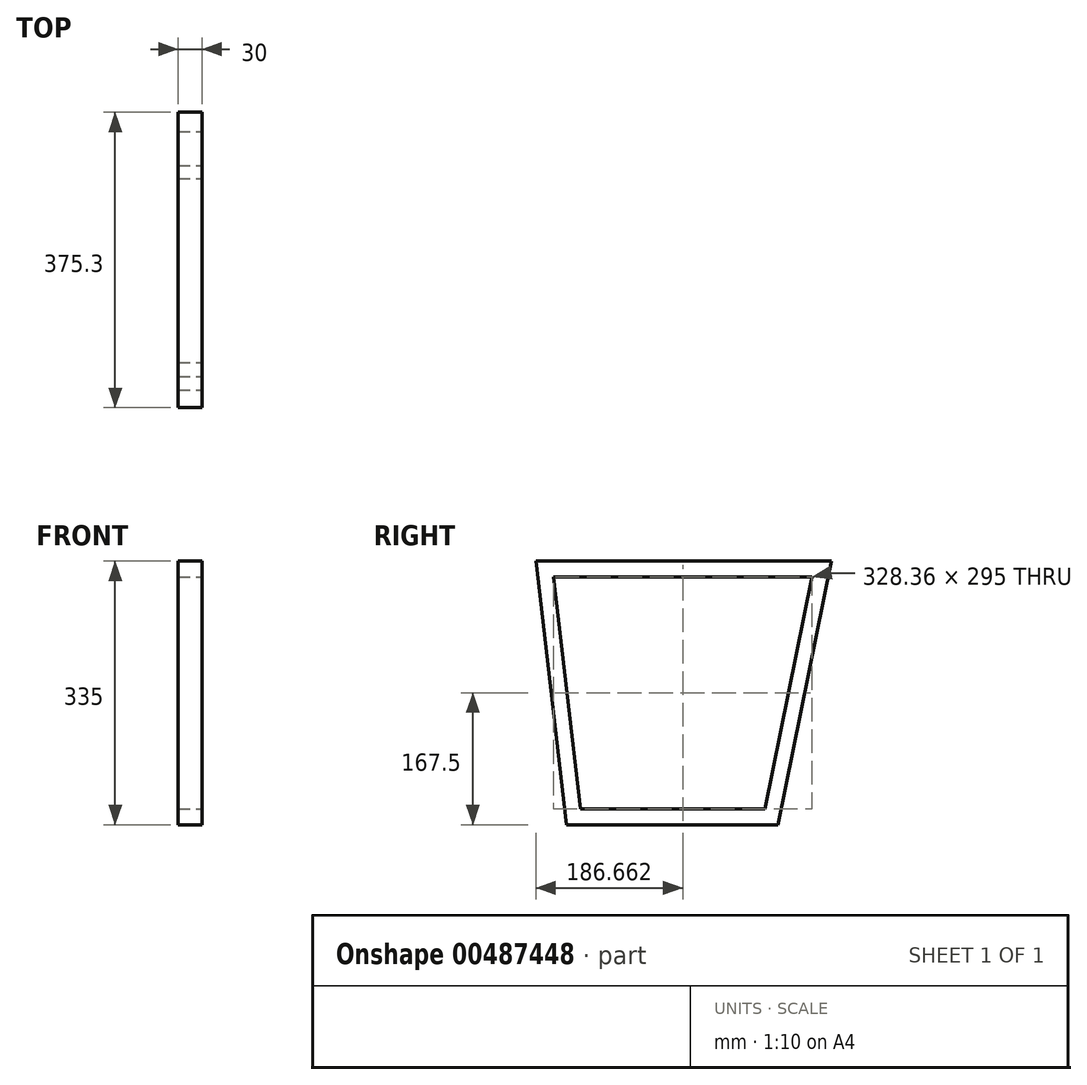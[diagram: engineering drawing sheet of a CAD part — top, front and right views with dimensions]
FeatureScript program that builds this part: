
annotation { "Feature Type Name" : "Feature", "Feature Type Description" : "" }
export const myFeature = defineFeature(function(context is Context, id is Id, definition is map)
    precondition{}
    {
        {
            var Q0;
            Q0=qCreatedBy(makeId("Right.planeOp"),FACE);
            var sketch = newSketch(context, id + "F0", { "sketchPlane" : qUnion([Q0])});
            skLineSegment(sketch, "E0", {"start": v(467.6, 335) * mm, "end": v(92.29, 335) * mm});
            skLineSegment(sketch, "E1", {"start": v(92.29, 335) * mm, "end": v(131.58, 0) * mm});
            skLineSegment(sketch, "E2", {"start": v(467.6, 335) * mm, "end": v(399.73, 0) * mm});
            skLineSegment(sketch, "E3", {"start": v(399.73, 0) * mm, "end": v(131.58, 0) * mm});
            skLineSegment(sketch, "E4.0", {"start": v(443.13, 315) * mm, "end": v(114.77, 315) * mm});
            skLineSegment(sketch, "E4.1", {"start": v(443.13, 315) * mm, "end": v(383.38, 20) * mm});
            skLineSegment(sketch, "E4.2", {"start": v(383.38, 20) * mm, "end": v(149.37, 20) * mm});
            skLineSegment(sketch, "E4.3", {"start": v(114.77, 315) * mm, "end": v(149.37, 20) * mm});
            skSolve(sketch);
        }
        {
            var Q0;
            Q0 = qSketchRegion(id + "F0", true);
            extrude(context, id + "F1", {"entities" : qUnion([Q0]), "oppositeDirection" : true, "depth" : 30 * mm});
        }
    });
